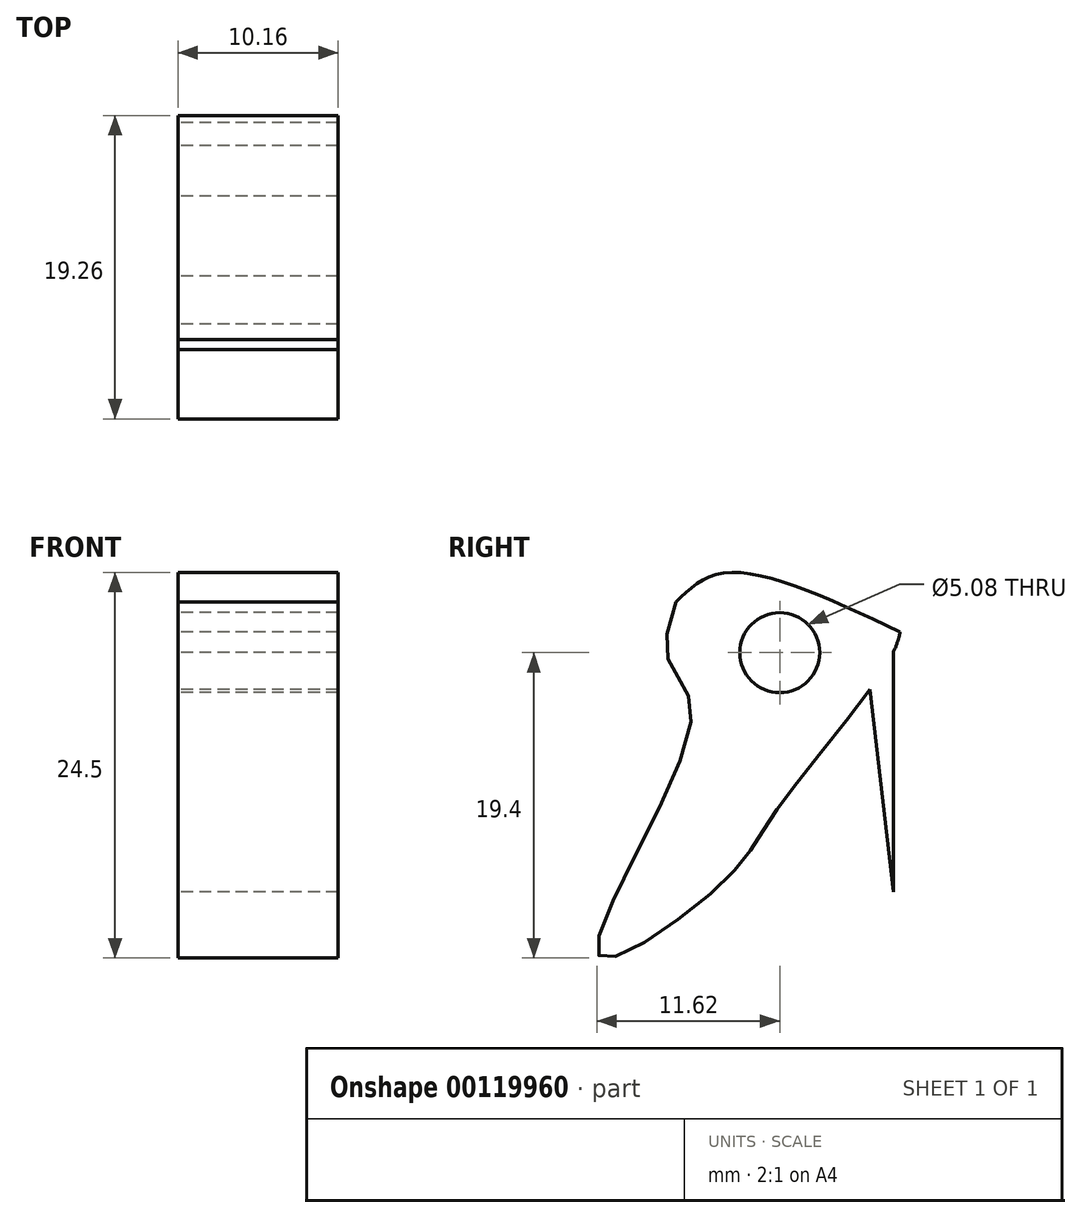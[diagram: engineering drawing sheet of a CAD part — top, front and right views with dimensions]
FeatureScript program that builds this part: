
annotation { "Feature Type Name" : "Feature", "Feature Type Description" : "" }
export const myFeature = defineFeature(function(context is Context, id is Id, definition is map)
    precondition{}
    {
        {
            var Q0;
            Q0=qCreatedBy(makeId("Right.planeOp"),FACE);
            var sketch = newSketch(context, id + "F0", { "sketchPlane" : qUnion([Q0])});
            skCircle(sketch, "E0", {"center": v(0, 0) * mm, "radius": 2.54 * mm});
            skFitSpline(sketch, "E1", {"points": [v(7.2, 0) * mm, v(7.92, 4.16) * mm, v(14.81, 17.32) * mm, v(19.7, 19.02) * mm, v(11.94, 19.9) * mm, v(0, 13.22) * mm, v(-7.19, 0) * mm, v(-5.61, -4.18) * mm, v(-11.53, -19.18) * mm, v(-3.62, -14.6) * mm, v(0, -9.72) * mm, v(7.2, 0) * mm]});
            skLineSegment(sketch, "E2", {"start": v(7.2, 0) * mm, "end": v(7.2, -15.2) * mm});
            skLineSegment(sketch, "E3", {"start": v(7.2, -15.2) * mm, "end": v(5.74, -2.34) * mm});
            skFitSpline(sketch, "E4", {"points": [v(-6.58, 3.22) * mm, v(-3.45, 5.08) * mm, v(7.64, 1.32) * mm], "startDerivative": vector(7.22, 7.17) * mm, "endDerivative": vector(19.98, -9.4) * mm});
            skSolve(sketch);
        }
        {
            var Q0;
            Q0=makeQuery(id+"F0.imprint","IMPRINT",FACE,{"disambiguationData":[TD([[makeQuery(id+"F0.imprint","IMPRINT",EDGE,{"derivedFrom":sQuery(id+"F0.wireOp",EDGE,"E0")}),-1.0]])]});
            var Q1;
            {var subQ0=sQuery(id+"F0.wireOp",EDGE,"E2");Q1=makeQuery(id+"F0.imprint","IMPRINT",FACE,{"disambiguationData":[TD([[makeQuery(id+"F0.imprint","IMPRINT",EDGE,{"derivedFrom":subQ0}),-1.0]])]});}
            extrude(context, id + "F1", {"entities" : qUnion([Q0, Q1]), "depth" : 5.08 * mm});
        }
        {
            var Q0;
            Q0=makeQuery(id+"F0.imprint","IMPRINT",FACE,{"disambiguationData":[TD([[makeQuery(id+"F0.imprint","IMPRINT",EDGE,{"derivedFrom":sQuery(id+"F0.wireOp",EDGE,"E0")}),-1.0]])]});
            var Q1;
            {var subQ0=sQuery(id+"F0.wireOp",EDGE,"E2");Q1=makeQuery(id+"F0.imprint","IMPRINT",FACE,{"disambiguationData":[TD([[makeQuery(id+"F0.imprint","IMPRINT",EDGE,{"derivedFrom":subQ0}),-1.0]])]});}
            extrude(context, id + "F2", {"entities" : qUnion([Q0, Q1]), "operationType" : NewBodyOperationType.ADD, "oppositeDirection" : true, "depth" : 5.08 * mm});
        }
    });
